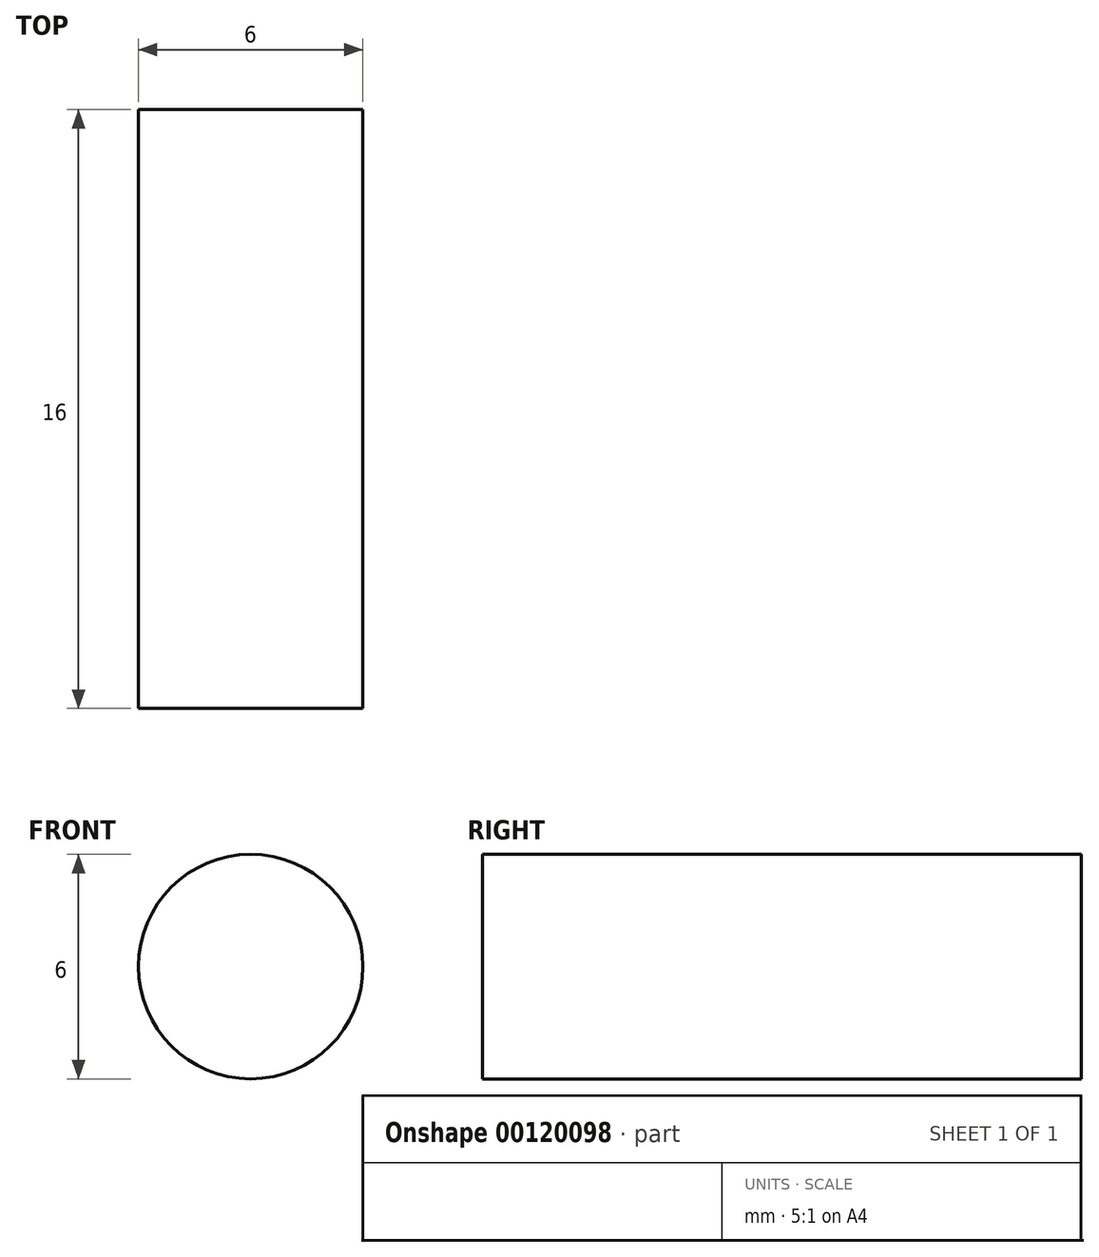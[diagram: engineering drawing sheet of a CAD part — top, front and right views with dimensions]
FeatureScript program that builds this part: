
annotation { "Feature Type Name" : "Feature", "Feature Type Description" : "" }
export const myFeature = defineFeature(function(context is Context, id is Id, definition is map)
    precondition{}
    {
        {
            var Q0;
            Q0=qCreatedBy(makeId("Front.planeOp"),FACE);
            var sketch = newSketch(context, id + "F0", { "sketchPlane" : qUnion([Q0])});
            skCircle(sketch, "E0", {"center": v(0, 0) * mm, "radius": 3 * mm});
            skSolve(sketch);
        }
        {
            var Q0;
            Q0 = qSketchRegion(id + "F0", true);
            extrude(context, id + "F1", {"entities" : qUnion([Q0]), "endBound" : BoundingType.SYMMETRIC, "depth" : 16 * mm});
        }
    });
